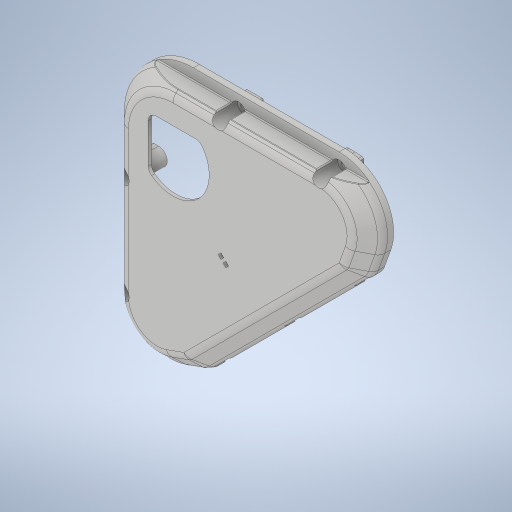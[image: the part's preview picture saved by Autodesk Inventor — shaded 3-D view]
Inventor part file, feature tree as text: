
AUTODESK INVENTOR PART (.ipt)
format: ipt  version: 2023.3 (Build 273359000, 359)  size: 578,560 bytes
history: native  units: in
note: dims shown in document units (in); Inventor stores cm internally (conversion verified against a paired STEP export)
features: sketch x2, extrude x1, hole x1, fillet x1
ambient origin geometry x8: Origin, YZ Plane, XZ Plane, XY Plane, X Axis, Y Axis, Z Axis, Center Point
bodies: Solid2 (feature_tree), Solid1 (feature_tree)
feature tree (5):
  extrude  "Extrusion1"  Depth=0.506in TaperAngle=0.0deg
  hole  "Hole1"  [1 undecoded]
  fillet  "Fillet1"  [1 undecoded]
  sketch  "Sketch1"  dims[d0=0.27in d1=0.506in d2=0.0in]
  sketch  "Sketch2"  dims[d3=0.18in d4=0.75in d5=0.35in d6=0.65in d7=0.563in d8=1.0in d9=0.8108in d10=0.025in]
note: 2 required parameter values undecoded (feature->parameter linkage not recoverable at this tier; creation-order binding heuristic only, values carry confidence <= 0.55)
